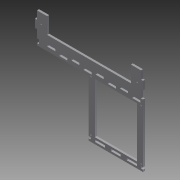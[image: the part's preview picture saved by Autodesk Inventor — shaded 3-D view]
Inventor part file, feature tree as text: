
AUTODESK INVENTOR PART (.ipt)
format: ipt  version: 2011 (Build 150239000, 239)  size: 522,240 bytes
history: native  units: in
note: dims shown in document units (in); Inventor stores cm internally (conversion verified against a paired STEP export)
features: extrude x18, sketch x18
ambient origin geometry x8: Origin, YZ Plane, XZ Plane, XY Plane, X Axis, Y Axis, Z Axis, Center Point
bodies: Solid1 (feature_tree)
feature tree (36):
  extrude  "Extrusion1"  Depth=6.75in
  extrude  "Extrusion2"  Depth=0.5in
  extrude  "Extrusion3"  Depth=0.5in
  extrude  "Extrusion4"  Depth=5.75in
  extrude  "Extrusion5"  Depth=0.5in
  extrude  "Extrusion6"  Depth=1.5in
  extrude  "Extrusion7"  Depth=1.5in
  extrude  "Extrusion8"  Depth=0.156in
  extrude  "Extrusion9"  Depth=0.25in TaperAngle=0.0deg
  extrude  "Extrusion10"  Depth=0.25in TaperAngle=0.0deg
  extrude  "Extrusion11"  Depth=0.25in TaperAngle=0.0deg
  extrude  "Extrusion12"  Depth=0.25in
  extrude  "Extrusion13"  Depth=0.25in
  extrude  "Extrusion14"  Depth=0.25in TaperAngle=0.0deg
  extrude  "Extrusion15"  Depth=3.0in
  extrude  "Extrusion16"  Depth=0.25in TaperAngle=0.0deg
  extrude  "Extrusion17"  Depth=1.0in
  extrude  "Extrusion18"  Depth=0.25in TaperAngle=0.0deg
  sketch  "Sketch1"  dims[d0=5.2in d1=6.75in]
  sketch  "Sketch2"  dims[d2=0.25in d3=0.5in]
  sketch  "Sketch3"  dims[d4=5.7in d5=0.5in]
  sketch  "Sketch4"  dims[d6=0.5in d7=5.75in]
  sketch  "Sketch5"  dims[d8=0.375in d9=0.5in]
  sketch  "Sketch6"  dims[d10=0.25in d11=1.5in]
  sketch  "Sketch7"  dims[d12=0.25in d13=1.5in]
  sketch  "Sketch8"  dims[d14=0.25in d15=0.156in]
  sketch  "Sketch9"  dims[d16=0.156in d17=0.25in d18=0.0in]
  sketch  "Sketch10"  dims[d19=0.125in d20=0.0in d21=0.25in d22=0.0in]
  sketch  "Sketch11"  dims[d23=0.25in d24=0.0in d25=0.25in d26=0.0in]
  sketch  "Sketch12"  dims[d27=0.25in d28=0.25in]
  sketch  "Sketch13"  dims[d29=0.25in d30=0.25in]
  sketch  "Sketch14"  dims[d31=0.25in d32=0.25in d33=0.0in]
  sketch  "Sketch15"  dims[d34=1.5in d35=3.0in]
  sketch  "Sketch16"  dims[d36=1.0in d37=0.25in d38=0.0in]
  sketch  "Sketch17"  dims[d39=6.65in d40=1.0in]
  sketch  "Sketch18"  dims[d41=1.5in d42=0.25in d43=0.0in d44=0.25in d45=0.0in d46=0.25in d47=0.0in d48=1.0in d49=0.25in d50=0.0in d51=0.25in d52=1.0in d53=0.25in d54=1.0in d55=0.25in d56=2.0in d57=1.0in d58=0.5in d59=1.0in d60=0.5in d61=1.0in d62=0.5in d63=1.0in d64=0.5in d65=1.0in d66=0.5in d67=1.0in d68=0.5in d69=1.0in d70=0.25in d71=0.0in d72=0.25in d73=1.0in d74=1.0in d75=0.25in d76=0.0in d77=0.25in d78=0.0in d79=0.25in d80=0.25in d81=0.0in d82=0.75in d83=0.156in d84=0.156in d85=0.25in d86=0.0in d87=0.25in d88=0.0in d89=1.0in d90=1.0in d91=1.0in d92=0.25in d93=0.0in]
